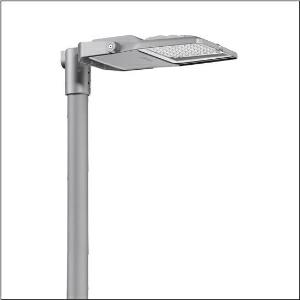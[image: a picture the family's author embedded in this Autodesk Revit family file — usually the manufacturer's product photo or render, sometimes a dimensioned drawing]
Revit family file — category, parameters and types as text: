
# Revit family: floodlight_fl_21_iq_mini___pl64_5xa7772c2e3a_d31a
name_source: partatom
category: Lighting Fixtures
units: mm (PartAtom-declared; Revit-internal decimal feet)

## family parameters
Cut with Voids When Loaded = No
Host = Face
Light Source = No
Part Type = Normal
Room Calculation Point = No
Round Connector Dimension = Use Diameter
Shared = No

## types (1)
- --- (1 x LED, 11790 lm, 87.2 W, 3000K)
    Apparent Load = 87 VA
    CIE Flux Codes = 28 80 98 100 100
    Color Rendering = 70
    Color Temperature = 3000K
    Default Elevation = 1800 mm
    Description = Floodlight FL 21 iQ mini, floodlight, primary light control with lens, of PMMA, primary optical cover: protective disc, of toughened safety glass, transparent, light distribution: PL64, light emission: direct distribution, installation type: surface-mounted, LED, High Power LED, rated luminous flux: 11.790lm, luminous efficacy: 135lm/W, light colour: 730, colour temperature: 3000K, control: Auto-Match, Temp-Guard, Night-Set, Smart-Wire, Desk-Remote (wireless, voltage-free reading and setting of iQ features in the workshop via application-optimized NFC function/RFID function), optimised constant luminous flux control (CLO 2.0), Light-Fading, Lumen-Switch, with terminal, 6-pole, mains connection: 220..240V, AC, 50/60Hz, start of lifetime: 87W, end of service life: 92W, reduction: 40W, luminaire housing, of diecast aluminium, powder-coated, Siteco® metallic grey (DB 702S), corrosivity category C5 mid according to DIN EN ISO 12944, sealing non-destructively replaceable, please order mast flange separately, mast bracket, of steel, galvanised, powder-coated, protection rating (complete): IP66, insulation class (complete): insulation class II (safety insulation), certification: CE, ENEC, VDE, protection symbol: D, impact resistance: IK08, permissible operating ambient temperature: -40..+40°C, permissible operating ambient temperature for outdoor applications: -40..+50°C, standard: DIN EN 12944, LABS conformity tested according to VDMA 24364:2018-05, packaging unit: 1 piece

Light Distribution: PL64
    Height = 70 mm
    Lamp = 1 x LED
    Lamp Light Flux = 11790 lm
    Lamp Power = 87.2 W
    Lamp count = 1
    Length = 485 mm
    Luminous efficacy = 135 lm/W
    Manufacturer = Siteco
    ModVariant = No
    Model = 5XA7772C2E3A
    Number of Poles = 1
    OnlyDefault = Yes
    Power Factor = 1
    Product Name = Floodlight FL 21 iQ mini | PL64
    Product group = floodlight | pylon annexe
    ProductGroupID = 6200
    Protection Class = Protection class II
    Protection Degree = IP 66
    RLX_Detail_Level = 1
    RLX_Emergency_Light_Flux = 0 lm
    RLX_Emergency_Type = 0
    RLX_Emergency_Type_DB = No
    RlxData = <blob elided: 101289 chars, md5=b89c3a88>
    Socket = socket
    Standby Power = 0 W
    System Light Flux = 11790 lm
    System Power = 87 W
    Type Comments = factory setting: luminous flux: 100 % | dim-lin: 254 | 456 mA
    Type Image = l_1007125.jpg
    URL = http://relux.com
    VarID = @adj_116513
    Voltage = 0 V
    Weight = 0.00 kg
    Width = 337 mm

## geometry (parser evidence)
native form markers: Blend x4, Sweep x12
no freeform markers — native parametric forms only
